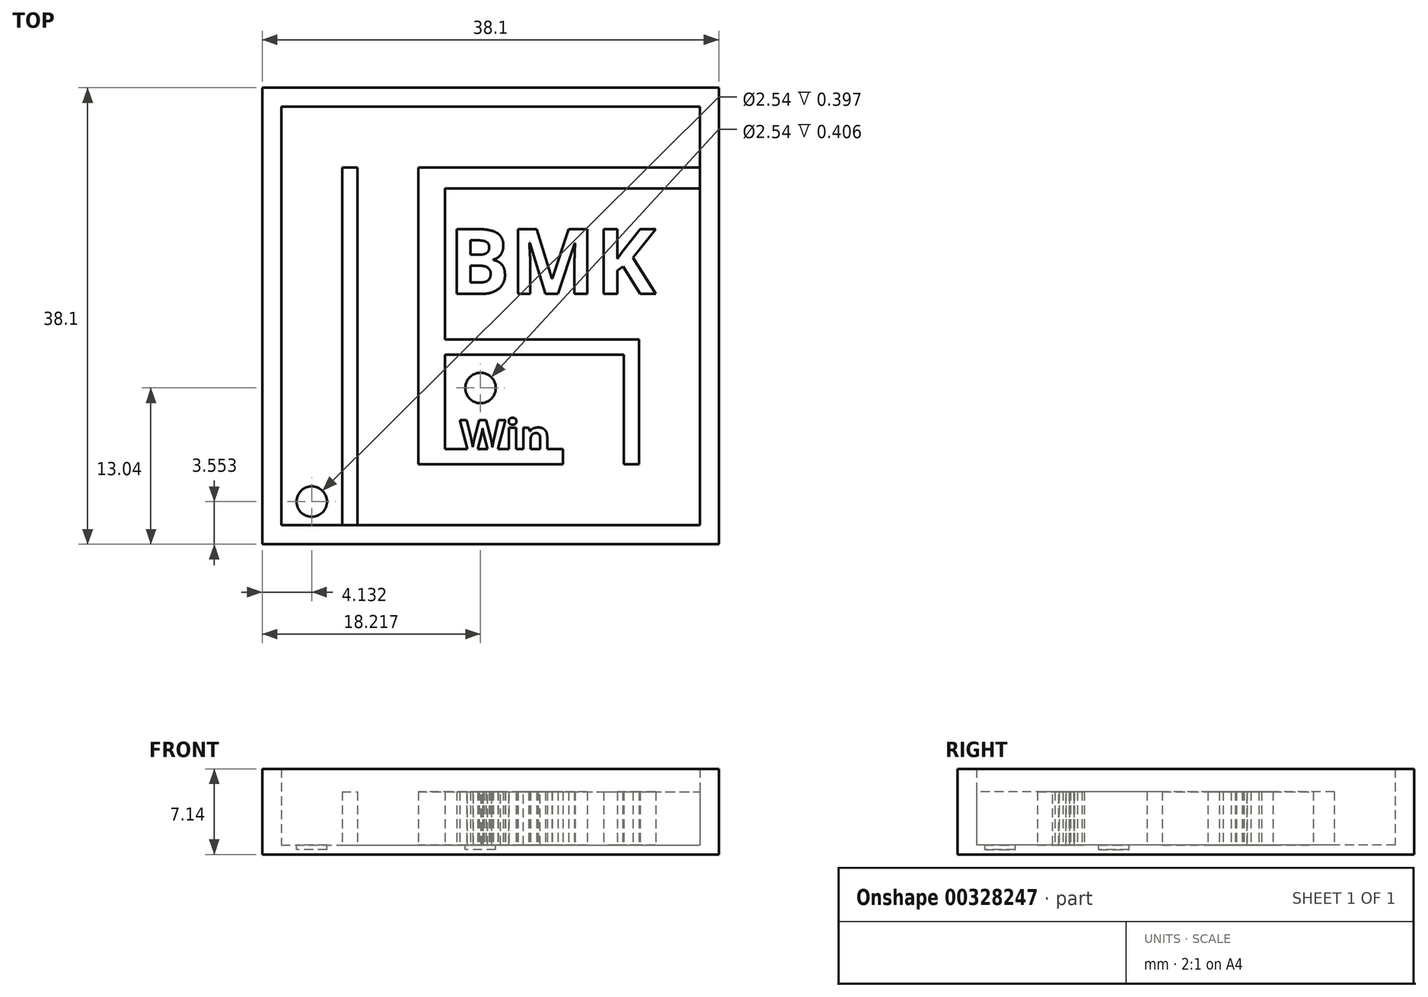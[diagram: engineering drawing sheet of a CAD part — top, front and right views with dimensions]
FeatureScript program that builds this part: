
annotation { "Feature Type Name" : "Feature", "Feature Type Description" : "" }
export const myFeature = defineFeature(function(context is Context, id is Id, definition is map)
    precondition{}
    {
        {
            var Q0;
            Q0=qCreatedBy(makeId("Top.planeOp"),FACE);
            var sketch = newSketch(context, id + "F0", { "sketchPlane" : qUnion([Q0])});
            skLineSegment(sketch, "E0.bottom", {"start": v(-20.35, 27.25) * mm, "end": v(17.75, 27.25) * mm});
            skLineSegment(sketch, "E0.top", {"start": v(-20.35, -10.85) * mm, "end": v(17.75, -10.85) * mm});
            skLineSegment(sketch, "E0.left", {"start": v(-20.35, 27.25) * mm, "end": v(-20.35, -10.85) * mm});
            skLineSegment(sketch, "E0.right", {"start": v(17.75, 27.25) * mm, "end": v(17.75, -10.85) * mm});
            skSolve(sketch);
        }
        {
            var Q0;
            Q0=makeQuery(id+"F0.imprint","IMPRINT",FACE,{"disambiguationData":[TD([[makeQuery(id+"F0.imprint","IMPRINT",EDGE,{"derivedFrom":sQuery(id+"F0.wireOp",EDGE,"E0.bottom")}),-1.0]])]});
            extrude(context, id + "F1", {"entities" : qUnion([Q0]), "depth" : 0.8 * mm});
        }
        {
            var Q0;
            Q0=makeQuery(id+"F1.opExtrude","CAP_FACE",FACE,{"disambiguationData":[OSD([sQuery(id+"F0.wireOp",EDGE,"E0.bottom"),sQuery(id+"F0.wireOp",EDGE,"E0.top"),sQuery(id+"F0.wireOp",EDGE,"E0.left"),sQuery(id+"F0.wireOp",EDGE,"E0.right")])],"isStart":false});
            var sketch = newSketch(context, id + "F2", { "sketchPlane" : qUnion([Q0])});
            skLineSegment(sketch, "E1.0", {"start": v(-18.76, 25.66) * mm, "end": v(16.17, 25.66) * mm});
            skLineSegment(sketch, "E1.1", {"start": v(-18.76, 25.66) * mm, "end": v(-18.76, -9.27) * mm});
            skLineSegment(sketch, "E1.2", {"start": v(-18.76, -9.27) * mm, "end": v(16.17, -9.27) * mm});
            skLineSegment(sketch, "E1.3", {"start": v(16.17, 25.66) * mm, "end": v(16.17, -9.27) * mm});
            skSolve(sketch);
        }
        {
            var Q0;
            Q0=makeQuery(id+"F2.imprint","IMPRINT",FACE,{"disambiguationData":[TD([[makeQuery(id+"F2.imprint","IMPRINT",EDGE,{"derivedFrom":sQuery(id+"F2.wireOp",EDGE,"E1.0")}),1.0]])]});
            extrude(context, id + "F3", {"entities" : qUnion([Q0]), "operationType" : NewBodyOperationType.ADD, "depth" : 6.35 * mm});
        }
        {
            var Q0;
            Q0=makeQuery(id+"F1.opExtrude","CAP_FACE",FACE,{"disambiguationData":[OSD([sQuery(id+"F0.wireOp",EDGE,"E0.bottom"),sQuery(id+"F0.wireOp",EDGE,"E0.top"),sQuery(id+"F0.wireOp",EDGE,"E0.left"),sQuery(id+"F0.wireOp",EDGE,"E0.right")])],"isStart":false});
            var sketch = newSketch(context, id + "F4", { "sketchPlane" : qUnion([Q0])});
            skLineSegment(sketch, "E2.bottom", {"start": v(-13.68, 20.58) * mm, "end": v(-12.4, 20.58) * mm});
            skLineSegment(sketch, "E2.top", {"start": v(-13.68, -9.27) * mm, "end": v(-12.4, -9.27) * mm});
            skLineSegment(sketch, "E2.left", {"start": v(-13.68, 20.58) * mm, "end": v(-13.68, -9.27) * mm});
            skLineSegment(sketch, "E2.right", {"start": v(-12.4, 20.58) * mm, "end": v(-12.4, -9.27) * mm});
            skSolve(sketch);
        }
        {
            var Q0;
            Q0=makeQuery(id+"F4.imprint","IMPRINT",FACE,{"disambiguationData":[TD([[makeQuery(id+"F4.imprint","IMPRINT",EDGE,{"derivedFrom":sQuery(id+"F4.wireOp",EDGE,"E2.bottom")}),-1.0]])]});
            extrude(context, id + "F5", {"entities" : qUnion([Q0]), "operationType" : NewBodyOperationType.ADD, "depth" : 4.44 * mm});
        }
        {
            var Q0;
            Q0=makeQuery(id+"F1.opExtrude","CAP_FACE",FACE,{"disambiguationData":[OSD([sQuery(id+"F0.wireOp",EDGE,"E0.bottom"),sQuery(id+"F0.wireOp",EDGE,"E0.top"),sQuery(id+"F0.wireOp",EDGE,"E0.left"),sQuery(id+"F0.wireOp",EDGE,"E0.right")])],"isStart":false});
            var sketch = newSketch(context, id + "F6", { "sketchPlane" : qUnion([Q0])});
            skLineSegment(sketch, "E3", {"start": v(-18.76, -9.27) * mm, "end": v(-13.68, -9.27) * mm});
            skCircle(sketch, "E4", {"center": v(-16.22, -7.3) * mm, "radius": 1.27 * mm});
            skPoint(sketch, "E4.centerSnap0", {"position": v(-16.22, -9.27) * mm});
            skSolve(sketch);
        }
        {
            var Q0;
            Q0=makeQuery(id+"F6.imprint","IMPRINT",FACE,{"disambiguationData":[TD([[makeQuery(id+"F6.imprint","IMPRINT",EDGE,{"derivedFrom":sQuery(id+"F6.wireOp",EDGE,"E4")}),1.0]])]});
            extrude(context, id + "F7", {"entities" : qUnion([Q0]), "operationType" : NewBodyOperationType.REMOVE, "oppositeDirection" : true, "depth" : 0.4 * mm});
        }
        {
            var Q0;
            Q0=makeQuery(id+"F1.opExtrude","CAP_FACE",FACE,{"disambiguationData":[OSD([sQuery(id+"F0.wireOp",EDGE,"E0.bottom"),sQuery(id+"F0.wireOp",EDGE,"E0.top"),sQuery(id+"F0.wireOp",EDGE,"E0.left"),sQuery(id+"F0.wireOp",EDGE,"E0.right")])],"isStart":false});
            var sketch = newSketch(context, id + "F8", { "sketchPlane" : qUnion([Q0])});
            skLineSegment(sketch, "E5.bottom", {"start": v(-7.33, 20.58) * mm, "end": v(16.17, 20.58) * mm});
            skLineSegment(sketch, "E5.left", {"start": v(-7.33, 20.58) * mm, "end": v(-7.33, 18.83) * mm});
            skLineSegment(sketch, "E5.right", {"start": v(16.17, 20.58) * mm, "end": v(16.17, 18.83) * mm});
            skLineSegment(sketch, "E6.left", {"start": v(-7.33, 18.83) * mm, "end": v(-7.33, 4.96) * mm});
            skLineSegment(sketch, "E7.bottom", {"start": v(-5.1, 4.96) * mm, "end": v(11.09, 4.96) * mm});
            skLineSegment(sketch, "E8.top", {"start": v(-5.1, -4.19) * mm, "end": v(-7.33, -4.19) * mm});
            skLineSegment(sketch, "E8.left", {"start": v(-5.1, 4.96) * mm, "end": v(-5.1, -2.92) * mm});
            skLineSegment(sketch, "E8.right", {"start": v(-7.33, 4.96) * mm, "end": v(-7.33, -4.19) * mm});
            skLineSegment(sketch, "E9.bottom", {"start": v(-5.1, -4.19) * mm, "end": v(4.74, -4.19) * mm});
            skLineSegment(sketch, "E9.top", {"start": v(-5.1, -2.92) * mm, "end": v(4.74, -2.92) * mm});
            skLineSegment(sketch, "E9.right", {"start": v(4.74, -4.19) * mm, "end": v(4.74, -2.92) * mm});
            skLineSegment(sketch, "E10.bottom", {"start": v(11.09, 4.96) * mm, "end": v(9.82, 4.96) * mm});
            skLineSegment(sketch, "E10.top", {"start": v(11.09, -4.19) * mm, "end": v(9.82, -4.19) * mm});
            skLineSegment(sketch, "E10.left", {"start": v(11.09, 4.96) * mm, "end": v(11.09, -4.19) * mm});
            skLineSegment(sketch, "E10.right", {"start": v(9.82, 4.96) * mm, "end": v(9.82, -4.19) * mm});
            skPoint(sketch, "E11.oppositeSnap0", {"position": v(-5.1, 13.24) * mm});
            skLineSegment(sketch, "E12.bottom", {"start": v(-3.36, 20.58) * mm, "end": v(-2.03, 20.58) * mm});
            skLineSegment(sketch, "E13.bottom", {"start": v(7.94, 20.58) * mm, "end": v(10.08, 20.58) * mm});
            skLineSegment(sketch, "E14.bottom", {"start": v(-0.03, 4.96) * mm, "end": v(2.6, 4.96) * mm});
            skPoint(sketch, "E15.orphan", {"position": v(-5.1, 21.52) * mm});
            skPoint(sketch, "E16.firstSnap0", {"position": v(-2.7, 20.58) * mm});
            skPoint(sketch, "E16.left.start.orphan", {"position": v(-2.7, 15.5) * mm});
            skText(sketch, "E17", { "text": "BMK", "fontName": "OpenSans-Bold.ttf"});
            skLineSegment(sketch, "E18", {"start": v(-5.1, 4.96) * mm, "end": v(-5.1, 18.83) * mm});
            skLineSegment(sketch, "E19", {"start": v(-5.1, 18.83) * mm, "end": v(16.17, 18.83) * mm});
            skLineSegment(sketch, "E20", {"start": v(-5.1, 4.96) * mm, "end": v(9.82, 4.96) * mm});
            skLineSegment(sketch, "E21", {"start": v(-5.1, 6.23) * mm, "end": v(11.09, 6.23) * mm});
            skLineSegment(sketch, "E22", {"start": v(11.09, 6.23) * mm, "end": v(11.09, 4.96) * mm});
            const initialGuessF8  = {"E17": [-0.00479, 0.01004, 1, 0, 0.00546]};
            skSetInitialGuess(sketch, initialGuessF8);
            skSolve(sketch);
        }
        {
            var Q0;
            Q0 = qSketchRegion(id + "F8", true);
            extrude(context, id + "F9", {"entities" : qUnion([Q0]), "operationType" : NewBodyOperationType.ADD, "depth" : 4.44 * mm});
        }
        {
            var Q0;
            {var subQ1=sQuery(id+"F8.wireOp",EDGE,"E5.left");Q0=makeQuery(id+"F8.imprint","IMPRINT",FACE,{"disambiguationData":[TD([[makeQuery(id+"F8.imprint","IMPRINT",EDGE,{"derivedFrom":subQ1}),-1.0]])]});}
            var sketch = newSketch(context, id + "F10", { "sketchPlane" : qUnion([Q0])});
            skCircle(sketch, "E23", {"center": v(-2.13, 2.2) * mm, "radius": 1.27 * mm});
            skSolve(sketch);
        }
        {
            var Q0;
            Q0 = qSketchRegion(id + "F10", true);
            extrude(context, id + "F11", {"entities" : qUnion([Q0]), "operationType" : NewBodyOperationType.REMOVE, "oppositeDirection" : true, "depth" : 0.4 * mm});
        }
        {
            var Q0;
            {var subQ1=sQuery(id+"F8.wireOp",EDGE,"E5.left");Q0=makeQuery(id+"F8.imprint","IMPRINT",FACE,{"disambiguationData":[TD([[makeQuery(id+"F8.imprint","IMPRINT",EDGE,{"derivedFrom":subQ1}),-1.0]])]});}
            var sketch = newSketch(context, id + "F12", { "sketchPlane" : qUnion([Q0])});
            skText(sketch, "E24", { "text": "Win", "fontName": "OpenSans-Bold.ttf"});
            const initialGuessF12  = {"E24": [-0.00386, -0.00329, 1, 0, 0.00283]};
            skSetInitialGuess(sketch, initialGuessF12);
            skSolve(sketch);
        }
        {
            var Q0;
            Q0 = qSketchRegion(id + "F12", true);
            extrude(context, id + "F13", {"entities" : qUnion([Q0]), "operationType" : NewBodyOperationType.ADD, "depth" : 4.44 * mm});
        }
    });
